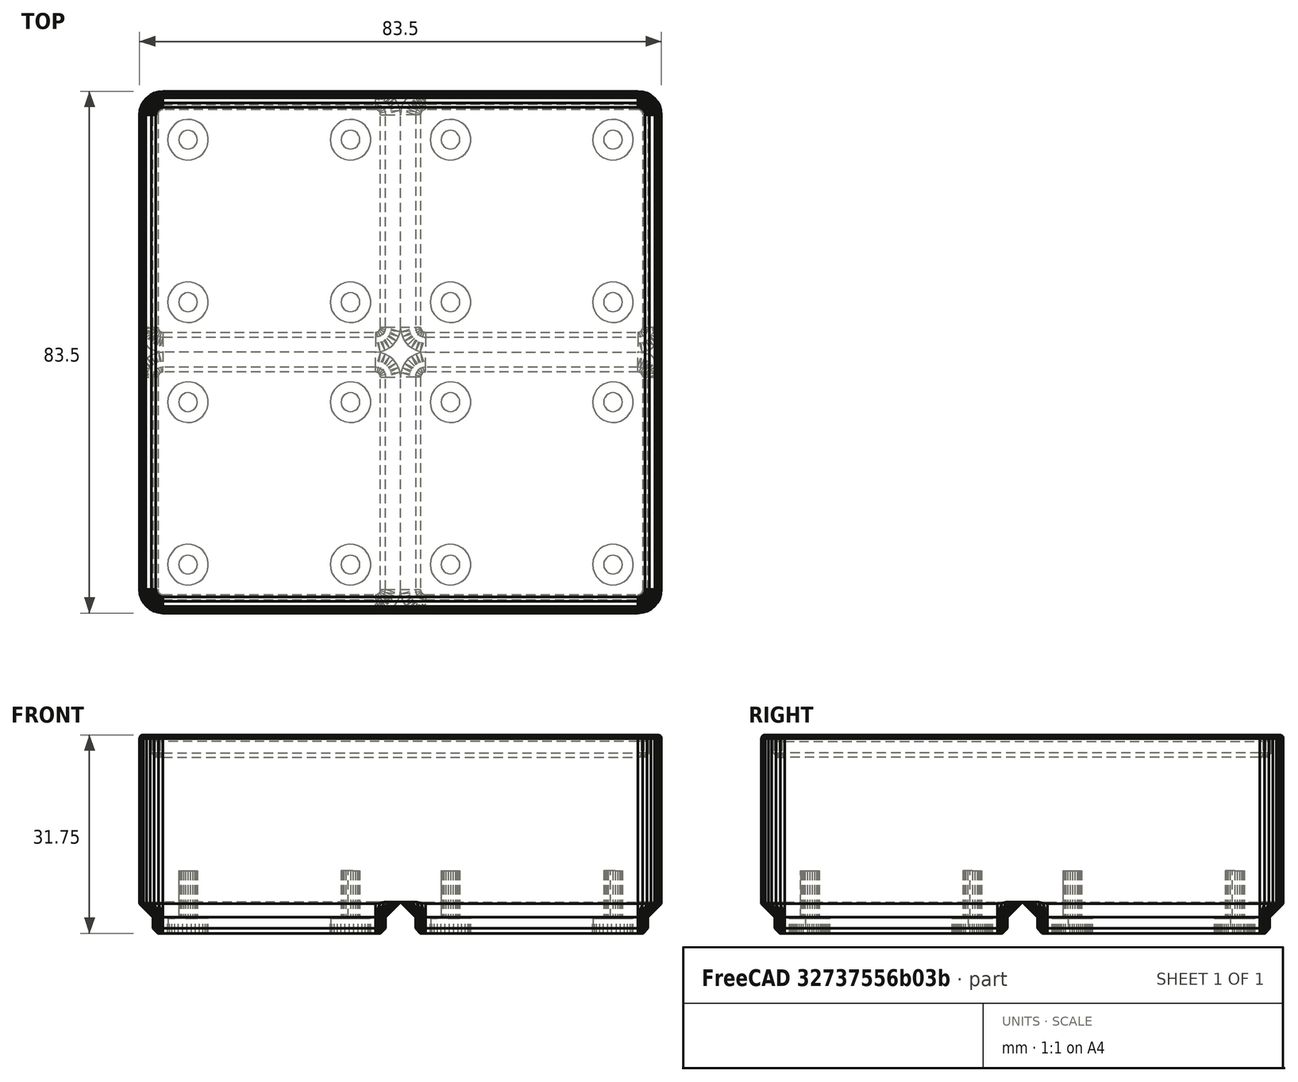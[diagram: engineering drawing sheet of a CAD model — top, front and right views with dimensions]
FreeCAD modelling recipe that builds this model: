
FCSTD DOCUMENT  (FreeCAD 0.20R29410 (Git))
Label: 2x2_plain
License: All rights reserved
LicenseURL: http://en.wikipedia.org/wiki/All_rights_reserved
objects: Part::Feature×2, Mesh::Feature×1, Part::Refine×1, PartDesign::FeatureBase×1, PartDesign::Body×1
note: 5 computed .brp shape members not serialized (recipe doc carries the construction recipe); baked Part::Feature solids carry a one-line shape summary decoded from their .brp

FEATURE [Mesh::Feature] _x2_Block_1_25in  label="2x2 Block 1.25in"
FEATURE [Part::Feature] _x2_Block_1_25in001
  shape: bbox 83.5 x 83.5 x 31.75 mm, 6748 faces, 0 solids (baked)
FEATURE [Part::Refine] _x2_Block_1_25in001001
  Source = -> _x2_Block_1_25in001
FEATURE [Part::Feature] _x2_Block_1_25in001001_solid  label="_x2_Block_1_25in001001 (Solid)"
  shape: bbox 83.5 x 83.5 x 31.75 mm, 2184 faces (baked)
FEATURE [PartDesign::FeatureBase] BaseFeature
  BaseFeature = -> _x2_Block_1_25in001001_solid
FEATURE [PartDesign::Body] Body
  BaseFeature = -> _x2_Block_1_25in001001_solid
  Group = -> [BaseFeature]
  Origin = -> Origin
  Tip = -> BaseFeature
